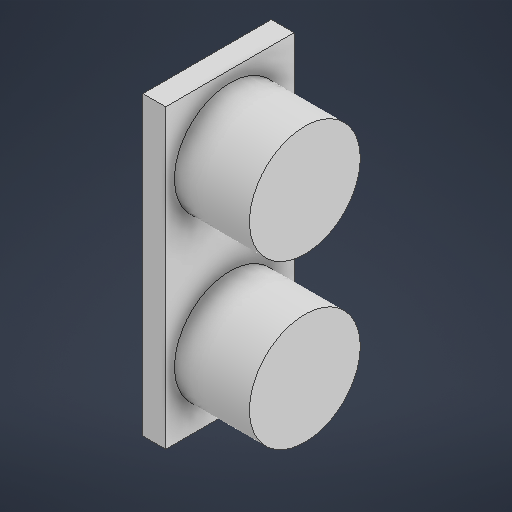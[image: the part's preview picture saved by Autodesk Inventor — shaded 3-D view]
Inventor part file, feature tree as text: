
AUTODESK INVENTOR PART (.ipt)
format: ipt  version: 2025.2 (Build 292293000, 293)  size: 212,992 bytes
history: native  units: mm
features: extrude x2, sketch x1
ambient origin geometry x8: Origin, YZ Plane, XZ Plane, XY Plane, X Axis, Y Axis, Z Axis, Center Point
bodies: Solid1 (feature_tree)
feature tree (3):
  sketch  "Sketch1"  dims[d0=45.5mm d1=17.0mm d3=42.0mm d4=19.7mm d5=3.5mm d6=0.0mm d7=11.5mm d8=0.0mm]
  extrude  "Extrusion1"  Depth=11.5mm
  extrude  "Extrusion2"  Depth=11.5mm
